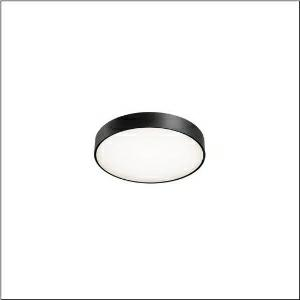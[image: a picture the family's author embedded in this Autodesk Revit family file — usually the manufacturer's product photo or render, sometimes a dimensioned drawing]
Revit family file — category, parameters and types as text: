
# Revit family: round_21_s_51mr34fd0421b
name_source: partatom
category: Lighting Fixtures
units: mm (PartAtom-declared; Revit-internal decimal feet)

## family parameters
Cut with Voids When Loaded = No
Host = Face
Light Source = No
Part Type = Normal
Room Calculation Point = No
Round Connector Dimension = Use Diameter
Shared = No

## types (1)
- Round 21 S (1 x LED, 3910 lm, 30.3 W, 4000K)
    Apparent Load = 30 VA
    CIE Flux Codes = 49 80 96 100 100
    Color Rendering = 80
    Color Temperature = 4000K
    Default Elevation = 1800 mm
    Description = Round 21 S, wall and ceiling luminaire, primary optical cover: cover, of PMMA, opal, light emission: direct distribution, primary light characteristic: symmetric, installation type: suspended mounting, surface-mounted, LED, rated luminous flux: 3.900lm, luminous efficacy: 129lm/W, light colour: 840, colour temperature: 4000K, control gear: DALI 2, with terminal, 5-pole, mains connection: 230V, AC, 50/60Hz, rated input power: 30.3W, housing, of aluminium, coated, black, diameter: 400mm, height: 62mm, protection rating (complete): IP40, insulation class (complete): insulation class I (protective earthing), certification: CE, impact resistance: IK04, permissible operating ambient temperature: -10..+35°C, packaging unit: 1 piece
    Height = 87 mm
    Lamp = 1 x LED
    Lamp Light Flux = 3910 lm
    Lamp Power = 30.3 W
    Lamp count = 1
    Length = 400 mm
    Luminous efficacy = 129 lm/W
    Manufacturer = Siteco
    ModVariant = No
    Model = 51MR34FD0421B
    Mounting Place = Ceiling
    Mounting Type = Surface mounted
    Number of Poles = 1
    OnlyDefault = Yes
    Power Factor = 1
    Product Name = Round 21 S
    Product group = wall and ceiling luminaire | ceiling mounted
    ProductGroupID = 305
    Protection Class = Protection class I
    Protection Degree = IP 40
    RLX_Detail_Level = 1
    RLX_Emergency_Light_Flux = 0 lm
    RLX_Emergency_Type = 0
    RLX_Emergency_Type_DB = No
    RlxData = <blob elided: 13465 chars, md5=08f38445>
    Socket = socket
    Standby Power = 0 W
    System Light Flux = 3910 lm
    System Power = 30 W
    Type Comments = Product without accessories
    Type Image = l_1258311.jpg
    URL = http://relux.com
    VarID = ---
    Voltage = 0 V
    Weight = 0.00 kg
    Width = 0 mm  [stored 0 ft]

note: [stored X ft] marks values corroborated as IEEE doubles in the binary element streams (Revit-internal decimal feet)

## geometry (parser evidence)
native form markers: Sweep x10
no freeform markers — native parametric forms only
